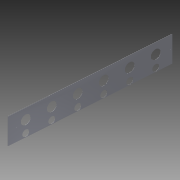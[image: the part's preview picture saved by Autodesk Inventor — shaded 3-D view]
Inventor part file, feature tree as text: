
AUTODESK INVENTOR PART (.ipt)
format: ipt  version: 2014 (Build 180170000, 170)  size: 227,840 bytes
history: native  units: in
note: dims shown in document units (in); Inventor stores cm internally (conversion verified against a paired STEP export)
features: sketch x6, hole x4, extrude x2, other x2, thicken_offset x1, sheet_metal_op x1
ambient origin geometry x8: Origin, YZ Plane, XZ Plane, XY Plane, X Axis, Y Axis, Z Axis, Center Point
bodies: Solid1 (feature_tree)
feature tree (16):
  thicken_offset  "Thicken1"
  sheet_metal_op  "Unfold4"
  hole  "spars"  [1 undecoded]
  hole  "supports"  [1 undecoded]
  hole  "rivets1"  [1 undecoded]
  hole  "Hole9"  [1 undecoded]
  extrude  "Extrusion4"  Depth=0.8108in
  sketch  "Sketch1"  dims[d0=-1.5665in d1=73.1722in d2=10.0in d3=0.0in]
  other  "2D Equation Curve1"
  other  "Srf1"
  sketch  "Sketch2"  dims[d4=0.06in d5=0.06in]
  sketch  "Sketch3"  dims[d6=3.5433in d7=5.9in]
  sketch  "Sketch19"  dims[d8=5.9624in d9=2.3622in d11=9.4248in d12=0.3937in d14=1.0in]
  sketch  "Sketch20"  dims[d16=3.5433in d17=0.75in d18=0.375in d19=0.25in d20=0.5635in d21=0.06in d22=0.8108in]
  sketch  "Sketch22"  dims[d23=2.4803in d24=1.3976in d25=2.3622in d27=9.4248in d28=0.3937in d30=1.0in d32=5.9624in d33=2.4803in d34=0.75in d35=0.375in d36=0.25in d37=0.5635in d38=0.06in d39=0.8108in d212=0.5in d213=1.0in d214=1.1811in d216=4.0in d217=0.3937in d219=1.0in d221=0.0394in d222=0.75in d223=0.375in d224=0.25in d225=0.5635in d226=0.06in d227=0.8108in d228=1.25in d230=1.0in d231=0.5in d232=1.1811in d234=4.0in d235=0.3937in d237=1.0in d239=1.5in d240=0.0394in d241=0.75in d242=0.375in d243=0.25in d244=0.5635in d245=0.06in d246=0.8108in d247=0.02in d248=5.9624in d249=0.1in d250=0.0in d255=4.1in d256=8.6024in d257=2.4815in]
  extrude  "ExtrusionSrf1"  Depth=1.3976in
note: 4 required parameter values undecoded (feature->parameter linkage not recoverable at this tier; creation-order binding heuristic only, values carry confidence <= 0.55)
